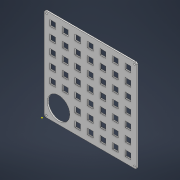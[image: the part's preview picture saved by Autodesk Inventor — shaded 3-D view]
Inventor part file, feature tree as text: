
AUTODESK INVENTOR PART (.ipt)
format: ipt  version: 2022 (Build 260153000, 153)  size: 297,472 bytes
history: native  units: mm
features: sketch x7, extrude x6, pattern_linear x2, fillet x2
ambient origin geometry x8: Origin, YZ Plane, XZ Plane, XY Plane, X Axis, Y Axis, Z Axis, Center Point
bodies: Solid1 (feature_tree)
feature tree (17):
  extrude  "Extrusion1"  Depth=220.0mm
  extrude  "Extrusion2"  Depth=3.0mm
  pattern_linear  "Rectangular Pattern1"  Count1=20  [1 undecoded]
  extrude  "Extrusion4"  Depth=28.5mm
  pattern_linear  "Rectangular Pattern2"  Count1=7 Spacing1=28.5mm
  extrude  "Extrusion5"  Depth=28.5mm
  sketch  "Sketch6"  dims[d14=50.0mm d16=28.5mm d17=200.0mm]
  extrude  "Extrusion3"  Depth=4.0mm
  fillet  "Fillet1"  Radius=55.0mm
  extrude  "Extrusion7"  Depth=4.0mm
  fillet  "Fillet2"  Radius=3.0mm
  sketch  "Sketch1"  dims[d0=220.0mm d1=220.0mm]
  sketch  "Sketch2"  dims[d2=3.0mm d3=0.0mm d4=200.0mm d5=200.0mm]
  sketch  "Sketch3"  dims[d6=28.5mm d7=28.5mm]
  sketch  "Sketch4"  dims[d8=20.5mm]
  sketch  "Sketch5"  dims[d9=3.0mm d10=0.0mm d11=70.0mm d13=28.5mm]
  sketch  "Sketch8"  dims[d18=200.0mm d19=55.0mm d20=55.0mm d21=51.0mm d22=3.0mm d23=0.0mm d24=200.0mm d25=200.0mm d26=28.5mm d27=20.5mm d28=3.0mm d29=0.0mm d30=20.0mm d32=28.5mm d33=50.0mm d35=28.5mm d36=5.0mm d37=5.0mm d38=3.0mm d39=10.0mm d40=0.0mm d41=13.0mm d42=13.0mm d43=13.0mm d44=13.0mm d58=2.0mm d59=200.0mm d60=200.0mm d61=210.0mm d62=210.0mm d63=3.5mm d64=20.0mm d66=200.0mm d67=20.0mm d69=200.0mm d72=10.0mm d73=0.0mm d74=4.0mm]
note: 1 required parameter value undecoded (feature->parameter linkage not recoverable at this tier; creation-order binding heuristic only, values carry confidence <= 0.55)
